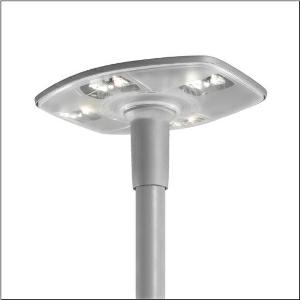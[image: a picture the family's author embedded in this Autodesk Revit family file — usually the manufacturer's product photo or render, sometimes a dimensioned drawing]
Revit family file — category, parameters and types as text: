
# Revit family: dl_r__30_led___st1_2c_5xa513271b08a5_992b
name_source: partatom
category: Lighting Fixtures
units: mm (PartAtom-declared; Revit-internal decimal feet)

## family parameters
Cut with Voids When Loaded = No
Host = Face
Light Source = No
Part Type = Normal
Room Calculation Point = No
Round Connector Dimension = Use Diameter
Shared = No

## types (1)
- --- (1 x LED, 5540 lm, 48.9 W, 4000K)
    Apparent Load = 49 VA
    CIE Flux Codes = 32 71 98 100 100
    Color Rendering = 70
    Color Temperature = 4000K
    Default Elevation = 1800 mm
    Description = DL® 30 LED, mast luminaire, primary light control with 3 zone facetted reflector, of plastic, aluminium vaporised, highly specular, primary optical cover: cover, of PMMA, structured, transparent, light distribution: ST1.2c, light emission: direct distribution, primary light characteristic: asymmetric, crossroads, installation type: post-top, LED, High Power LED, rated luminous flux: 5.540lm, luminous efficacy: 113lm/W, light colour: 740, colour temperature: 4000K, control gear: ECG Plus, control: flexible luminous flux parameterisation, time-dependent luminous flux control, constant luminous flux control, digital communication interface, power reduction, electronic power reduction, mains connection: 230..240V, AC, 50/60Hz, start of lifetime: 49W, end of service life: 51W, reduction: 23W, luminaire housing, of diecast aluminium, powder-coated, Siteco® metallic grey (DB 702S), length: 600mm, width: 510mm, height: 290mm, spigot size: d x l = 76 x 100mm (post-top) | with reducer (optional accessory) 60 x 100mm, protection rating (complete): IP66, insulation class (complete): insulation class II (safety insulation), certification: CE, ENEC, VDE, impact resistance: IK08, permissible operating ambient temperature: -25..+30°C, standard-compliant lighting for roads and squares, packaging unit: 1 piece

Light Distribution: ST1.2c
    Height = 290 mm
    Lamp = 1 x LED
    Lamp Light Flux = 5540 lm
    Lamp Power = 48.9 W
    Lamp count = 1
    Length = 510 mm
    Luminous efficacy = 113 lm/W
    Manufacturer = Siteco
    ModVariant = No
    Model = 5XA513271B08A5
    Number of Poles = 1
    OnlyDefault = Yes
    Power Factor = 1
    Product Name = DL® 30 LED | ST1.2c
    Product group = mast luminaire | pylon top
    ProductGroupID = 6100
    Protection Class = Protection class II
    Protection Degree = IP 66
    RLX_Detail_Level = 1
    RLX_Emergency_Light_Flux = 0 lm
    RLX_Emergency_Type = 0
    RLX_Emergency_Type_DB = No
    RlxData = <blob elided: 86445 chars, md5=a50b342b>
    Socket = socket
    Standby Power = 0 W
    System Light Flux = 5540 lm
    System Power = 49 W
    Type Comments = factory setting: luminous flux: 100 % | dim-lin: 254 | 497 mA
    Type Image = l_1006003.jpg
    URL = http://relux.com
    VarID = @adj_172255
    Voltage = 0 V
    Weight = 0.00 kg
    Width = 600 mm

## geometry (parser evidence)
native form markers: Blend x4, Sweep x12
no freeform markers — native parametric forms only
